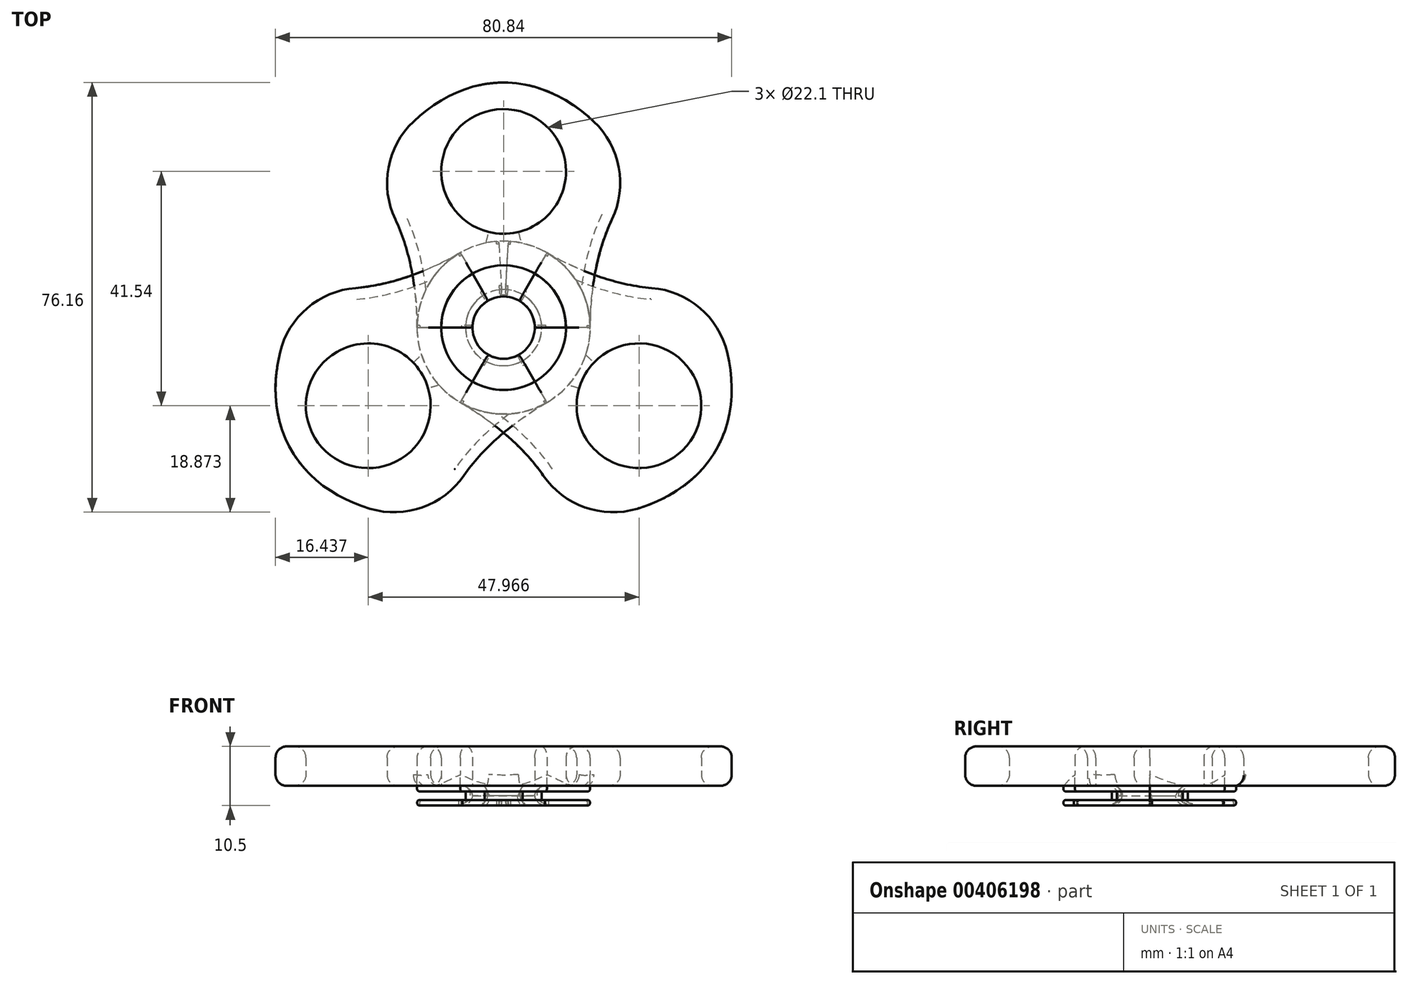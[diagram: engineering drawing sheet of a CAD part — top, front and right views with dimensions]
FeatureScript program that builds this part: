
annotation { "Feature Type Name" : "Feature", "Feature Type Description" : "" }
export const myFeature = defineFeature(function(context is Context, id is Id, definition is map)
    precondition{}
    {
        {
            var Q0;
            Q0=qCreatedBy(makeId("Top.planeOp"),FACE);
            var sketch = newSketch(context, id + "F0", { "sketchPlane" : qUnion([Q0])});
            skCircle(sketch, "E0", {"center": v(0, 0) * mm, "radius": 11.05 * mm});
            skEllipse(sketch, "E1", {"center": v(0, 0) * mm, "majorRadius": 43.44 * mm, "minorRadius": 29.52 * mm, "majorAxis": v(0, 1)});
            skEllipse(sketch, "E2", {"center": v(29.52, 0) * mm, "majorRadius": 28 * mm, "minorRadius": 14.19 * mm, "majorAxis": v(0, -1)});
            skLineSegment(sketch, "E3", {"start": v(0, 58.33) * mm, "end": v(0, -59.11) * mm});
            skEllipse(sketch, "E4", {"center": v(-29.52, 0) * mm, "majorRadius": 27.94 * mm, "minorRadius": 14.94 * mm, "majorAxis": v(0, 1)});
            skCircle(sketch, "E5", {"center": v(0, 27.7) * mm, "radius": 11.05 * mm});
            skLineSegment(sketch, "E6", {"start": v(54.05, 0) * mm, "end": v(-64.12, 0) * mm});
            skCircle(sketch, "E7", {"center": v(0, 0) * mm, "radius": 5.5 * mm});
            skCircle(sketch, "E8", {"center": v(0, 0) * mm, "radius": 15.34 * mm});
            skCircle(sketch, "E9", {"center": v(0, 0) * mm, "radius": 6.75 * mm});
            skSolve(sketch);
        }
        {
            var Q0;
            {var subQ1=sQuery(id+"F0.wireOp",EDGE,"E3");var subQ5=sQuery(id+"F0.wireOp",EDGE,"E0");var subQ6=makeQuery(id+"F0.imprint","INTERSECT",VERTEX,{"disambiguationData":[OD(0.0)],"derivedFrom":[subQ5,subQ1]});Q0=makeQuery(id+"F0.imprint","IMPRINT",FACE,{"disambiguationData":[TD([[makeQuery(id+"F0.imprint","IMPRINT",EDGE,{"disambiguationData":[TD([[subQ6,1.0]])],"derivedFrom":subQ5}),-1.0]])]});}
            var Q1;
            {var subQ1=sQuery(id+"F0.wireOp",EDGE,"E3");var subQ6=sQuery(id+"F0.wireOp",EDGE,"E1");var subQ9=makeQuery(id+"F0.imprint","INTERSECT",VERTEX,{"disambiguationData":[OD(0.0)],"derivedFrom":[subQ6,subQ1]});Q1=makeQuery(id+"F0.imprint","IMPRINT",FACE,{"disambiguationData":[TD([[makeQuery(id+"F0.imprint","IMPRINT",EDGE,{"disambiguationData":[TD([[subQ9,1.0]])],"derivedFrom":subQ6}),1.0]])]});}
            extrude(context, id + "F1", {"entities" : qUnion([Q0, Q1]), "depth" : 7 * mm});
        }
        {
            var Q0;
            {var subQ0=sQuery(id+"F0.wireOp",EDGE,"E3");var subQ1=sQuery(id+"F0.wireOp",EDGE,"E0");var subQ2=makeQuery(id+"F0.imprint","INTERSECT",VERTEX,{"disambiguationData":[OD(0.0)],"derivedFrom":[subQ1,subQ0]});Q0=makeQuery(id+"F0.imprint","IMPRINT",FACE,{"disambiguationData":[TD([[makeQuery(id+"F0.imprint","IMPRINT",EDGE,{"disambiguationData":[TD([[subQ2,1.0]])],"derivedFrom":subQ1}),-1.0]])]});}
            var Q1;
            {var subQ0=sQuery(id+"F0.wireOp",EDGE,"E3");var subQ1=sQuery(id+"F0.wireOp",EDGE,"E0");var subQ2=makeQuery(id+"F0.imprint","INTERSECT",VERTEX,{"disambiguationData":[OD(0.0)],"derivedFrom":[subQ1,subQ0]});Q1=makeQuery(id+"F0.imprint","IMPRINT",FACE,{"disambiguationData":[TD([[makeQuery(id+"F0.imprint","IMPRINT",EDGE,{"disambiguationData":[TD([[subQ2,1.0]])],"derivedFrom":subQ1}),1.0]])]});}
            var Q2;
            {var subQ0=sQuery(id+"F0.wireOp",EDGE,"E9");var subQ1=sQuery(id+"F0.wireOp",EDGE,"E3");var subQ2=makeQuery(id+"F0.imprint","INTERSECT",VERTEX,{"disambiguationData":[OD(0.0)],"derivedFrom":[subQ1,subQ0]});Q2=makeQuery(id+"F0.imprint","IMPRINT",FACE,{"disambiguationData":[TD([[makeQuery(id+"F0.imprint","IMPRINT",EDGE,{"disambiguationData":[TD([[subQ2,-1.0]])],"derivedFrom":subQ1}),1.0]])]});}
            extrude(context, id + "F2", {"entities" : qUnion([Q0, Q1, Q2]), "operationType" : NewBodyOperationType.ADD, "oppositeDirection" : true, "depth" : 1 * mm});
        }
        {
            var Q0;
            {var subQ0=sQuery(id+"F0.wireOp",EDGE,"E9");var subQ1=sQuery(id+"F0.wireOp",EDGE,"E3");var subQ2=makeQuery(id+"F0.imprint","INTERSECT",VERTEX,{"disambiguationData":[OD(0.0)],"derivedFrom":[subQ1,subQ0]});Q0=makeQuery(id+"F0.imprint","IMPRINT",FACE,{"disambiguationData":[TD([[makeQuery(id+"F0.imprint","IMPRINT",EDGE,{"disambiguationData":[TD([[subQ2,-1.0]])],"derivedFrom":subQ1}),1.0]])]});}
            extrude(context, id + "F3", {"entities" : qUnion([Q0]), "operationType" : NewBodyOperationType.ADD, "oppositeDirection" : true, "depth" : 2.5 * mm});
        }
        {
            var Q0;
            {var subQ0=sQuery(id+"F0.wireOp",EDGE,"E9");var subQ1=sQuery(id+"F0.wireOp",EDGE,"E3");var subQ2=makeQuery(id+"F0.imprint","INTERSECT",VERTEX,{"disambiguationData":[OD(0.0)],"derivedFrom":[subQ1,subQ0]});Q0=makeQuery(id+"F0.imprint","IMPRINT",FACE,{"disambiguationData":[TD([[makeQuery(id+"F0.imprint","IMPRINT",EDGE,{"disambiguationData":[TD([[subQ2,-1.0]])],"derivedFrom":subQ1}),1.0]])]});}
            var Q1;
            {var subQ0=sQuery(id+"F0.wireOp",EDGE,"E3");var subQ1=sQuery(id+"F0.wireOp",EDGE,"E0");var subQ2=makeQuery(id+"F0.imprint","INTERSECT",VERTEX,{"disambiguationData":[OD(0.0)],"derivedFrom":[subQ1,subQ0]});Q1=makeQuery(id+"F0.imprint","IMPRINT",FACE,{"disambiguationData":[TD([[makeQuery(id+"F0.imprint","IMPRINT",EDGE,{"disambiguationData":[TD([[subQ2,1.0]])],"derivedFrom":subQ1}),1.0]])]});}
            var Q2;
            {var subQ0=sQuery(id+"F0.wireOp",EDGE,"E3");var subQ1=sQuery(id+"F0.wireOp",EDGE,"E0");var subQ2=makeQuery(id+"F0.imprint","INTERSECT",VERTEX,{"disambiguationData":[OD(0.0)],"derivedFrom":[subQ1,subQ0]});Q2=makeQuery(id+"F0.imprint","IMPRINT",FACE,{"disambiguationData":[TD([[makeQuery(id+"F0.imprint","IMPRINT",EDGE,{"disambiguationData":[TD([[subQ2,1.0]])],"derivedFrom":subQ1}),-1.0]])]});}
            extrude(context, id + "F4", {"entities" : qUnion([Q0, Q1, Q2]), "operationType" : NewBodyOperationType.ADD, "oppositeDirection" : true, "depth" : 3.5 * mm, "hasSecondDirection" : true, "secondDirectionOppositeDirection" : true, "secondDirectionDepth" : 2.5 * mm});
        }
        {
            var Q0;
            Q0=makeQuery(id+"F1.opExtrude","SWEPT_BODY",BODY,{"disambiguationData":[OSD([sQuery(id+"F0.wireOp",EDGE,"E0"),sQuery(id+"F0.wireOp",EDGE,"E1"),sQuery(id+"F0.wireOp",EDGE,"E2"),sQuery(id+"F0.wireOp",EDGE,"E3"),sQuery(id+"F0.wireOp",EDGE,"E5"),sQuery(id+"F0.wireOp",EDGE,"E6")])]});
            var Q1;
            Q1=qCreatedBy(makeId("Right.planeOp"),FACE);
            mirror(context, id + "F5", {"operationType" : NewBodyOperationType.ADD, "entities" : qUnion([Q0]), "mirrorPlane" : qUnion([Q1])});
        }
        {
            var Q0;
            {var subQ0=sQuery(id+"F0.wireOp",EDGE,"E6");var subQ1=sQuery(id+"F0.wireOp",EDGE,"E3");var subQ2=makeQuery(id+"F0.imprint","INTERSECT",VERTEX,{"derivedFrom":[subQ1,subQ0]});Q0=makeQuery(id+"F0.imprint","IMPRINT",FACE,{"disambiguationData":[TD([[makeQuery(id+"F0.imprint","IMPRINT",EDGE,{"disambiguationData":[TD([[subQ2,-1.0]])],"derivedFrom":subQ1}),-1.0]])]});}
            var Q1;
            {var subQ0=sQuery(id+"F0.wireOp",EDGE,"E7");var subQ1=sQuery(id+"F0.wireOp",EDGE,"E3");var subQ2=makeQuery(id+"F0.imprint","INTERSECT",VERTEX,{"disambiguationData":[OD(0.0)],"derivedFrom":[subQ1,subQ0]});Q1=makeQuery(id+"F0.imprint","IMPRINT",FACE,{"disambiguationData":[TD([[makeQuery(id+"F0.imprint","IMPRINT",EDGE,{"disambiguationData":[TD([[subQ2,-1.0]])],"derivedFrom":subQ1}),-1.0]])]});}
            var Q2;
            {var subQ0=sQuery(id+"F0.wireOp",EDGE,"E7");var subQ1=sQuery(id+"F0.wireOp",EDGE,"E3");var subQ2=makeQuery(id+"F0.imprint","INTERSECT",VERTEX,{"disambiguationData":[OD(0.0)],"derivedFrom":[subQ1,subQ0]});Q2=makeQuery(id+"F0.imprint","IMPRINT",FACE,{"disambiguationData":[TD([[makeQuery(id+"F0.imprint","IMPRINT",EDGE,{"disambiguationData":[TD([[subQ2,-1.0]])],"derivedFrom":subQ1}),1.0]])]});}
            var Q3;
            {var subQ0=sQuery(id+"F0.wireOp",EDGE,"E6");var subQ1=sQuery(id+"F0.wireOp",EDGE,"E3");var subQ2=makeQuery(id+"F0.imprint","INTERSECT",VERTEX,{"derivedFrom":[subQ1,subQ0]});Q3=makeQuery(id+"F0.imprint","IMPRINT",FACE,{"disambiguationData":[TD([[makeQuery(id+"F0.imprint","IMPRINT",EDGE,{"disambiguationData":[TD([[subQ2,-1.0]])],"derivedFrom":subQ1}),1.0]])]});}
            extrude(context, id + "F6", {"entities" : qUnion([Q0, Q1, Q2, Q3]), "depth" : 22.66 * mm, "hasSecondDirection" : true, "secondDirectionOppositeDirection" : false, "secondDirectionDepth" : 15.2 * mm});
        }
        {
            var Q0;
            {var subQ0=makeQuery(id+"F4.opExtrude","CAP_FACE",FACE,{"disambiguationData":[OSD([sQuery(id+"F0.wireOp",EDGE,"E3"),sQuery(id+"F0.wireOp",EDGE,"E6"),sQuery(id+"F0.wireOp",EDGE,"E7"),sQuery(id+"F0.wireOp",EDGE,"E8")])],"isStart":false});Q0=makeQuery(id+"F5.boolean.opBoolean","MERGE",FACE,{"derivedFrom":[subQ0,makeQuery(id+"F5.opPattern","COPY",FACE,{"derivedFrom":subQ0,"instanceName":"1"})]});}
            var sketch = newSketch(context, id + "F7", { "sketchPlane" : qUnion([Q0])});
            skLineSegment(sketch, "E10", {"start": v(0, -18) * mm, "end": v(-1, -18) * mm});
            skLineSegment(sketch, "E11", {"start": v(-1, -18) * mm, "end": v(0, 0) * mm});
            skLineSegment(sketch, "E12", {"start": v(0, 0) * mm, "end": v(1, -18) * mm});
            skLineSegment(sketch, "E13", {"start": v(1, -18) * mm, "end": v(0, -18) * mm});
            skSolve(sketch);
        }
        {
            var Q0;
            {var subQ0=makeQuery(id+"F1.opExtrude","CAP_EDGE",EDGE,{"disambiguationData":[OSD([sQuery(id+"F0.wireOp",EDGE,"E5")])],"isStart":true});Q0=makeQuery(id+"F5.boolean.opBoolean","MERGE",EDGE,{"derivedFrom":[subQ0,makeQuery(id+"F5.opPattern","COPY",EDGE,{"derivedFrom":subQ0,"instanceName":"1"})]});}
            var Q1;
            Q1=makeQuery(id+"F1.opExtrude","CAP_EDGE",EDGE,{"disambiguationData":[OSD([sQuery(id+"F0.wireOp",EDGE,"E2")])],"isStart":true});
            var Q2;
            Q2=makeQuery(id+"F1.opExtrude","CAP_EDGE",EDGE,{"disambiguationData":[OSD([sQuery(id+"F0.wireOp",EDGE,"E2")])],"isStart":false});
            var Q3;
            Q3=makeQuery(id+"F5.opPattern","COPY",EDGE,{"derivedFrom":makeQuery(id+"F1.opExtrude","CAP_EDGE",EDGE,{"disambiguationData":[OSD([sQuery(id+"F0.wireOp",EDGE,"E2")])],"isStart":true}),"instanceName":"1"});
            var Q4;
            {var subQ0=makeQuery(id+"F1.opExtrude","CAP_EDGE",EDGE,{"disambiguationData":[OSD([sQuery(id+"F0.wireOp",EDGE,"E1")])],"isStart":true});Q4=makeQuery(id+"F5.boolean.opBoolean","MERGE",EDGE,{"derivedFrom":[subQ0,makeQuery(id+"F5.opPattern","COPY",EDGE,{"derivedFrom":subQ0,"instanceName":"1"})]});}
            var Q5;
            {var subQ0=makeQuery(id+"F4.opExtrude","CAP_EDGE",EDGE,{"disambiguationData":[OSD([sQuery(id+"F0.wireOp",EDGE,"E7")])],"isStart":false});Q5=makeQuery(id+"F5.boolean.opBoolean","MERGE",EDGE,{"derivedFrom":[subQ0,makeQuery(id+"F5.opPattern","COPY",EDGE,{"derivedFrom":subQ0,"instanceName":"1"})]});}
            var Q6;
            {var subQ0=makeQuery(id+"F2.opExtrude","CAP_EDGE",EDGE,{"disambiguationData":[OSD([sQuery(id+"F0.wireOp",EDGE,"E7")])],"isStart":true});Q6=makeQuery(id+"F5.boolean.opBoolean","MERGE",EDGE,{"derivedFrom":[subQ0,makeQuery(id+"F5.opPattern","COPY",EDGE,{"derivedFrom":subQ0,"instanceName":"1"})]});}
            var Q7;
            {var subQ0=makeQuery(id+"F1.opExtrude","CAP_EDGE",EDGE,{"disambiguationData":[OSD([sQuery(id+"F0.wireOp",EDGE,"E1")])],"isStart":false});Q7=makeQuery(id+"F5.boolean.opBoolean","MERGE",EDGE,{"derivedFrom":[subQ0,makeQuery(id+"F5.opPattern","COPY",EDGE,{"derivedFrom":subQ0,"instanceName":"1"})]});}
            var Q8;
            {var subQ0=makeQuery(id+"F1.opExtrude","CAP_EDGE",EDGE,{"disambiguationData":[OSD([sQuery(id+"F0.wireOp",EDGE,"E5")])],"isStart":false});Q8=makeQuery(id+"F5.boolean.opBoolean","MERGE",EDGE,{"derivedFrom":[subQ0,makeQuery(id+"F5.opPattern","COPY",EDGE,{"derivedFrom":subQ0,"instanceName":"1"})]});}
            var Q9;
            {var subQ0=makeQuery(id+"F1.opExtrude","CAP_EDGE",EDGE,{"disambiguationData":[OSD([sQuery(id+"F0.wireOp",EDGE,"E0")])],"isStart":false});Q9=makeQuery(id+"F5.boolean.opBoolean","MERGE",EDGE,{"derivedFrom":[subQ0,makeQuery(id+"F5.opPattern","COPY",EDGE,{"derivedFrom":subQ0,"instanceName":"1"})]});}
            var Q10;
            Q10=makeQuery(id+"F5.opPattern","COPY",EDGE,{"derivedFrom":makeQuery(id+"F1.opExtrude","CAP_EDGE",EDGE,{"disambiguationData":[OSD([sQuery(id+"F0.wireOp",EDGE,"E2")])],"isStart":false}),"instanceName":"1"});
            fillet(context, id + "F8", {"entities" : qUnion([Q0, Q1, Q2, Q3, Q4, Q5, Q6, Q7, Q8, Q9, Q10]), "radius" : 2 * mm, "tangentPropagation" : true, "allowEdgeOverflow" : false});
        }
        {
            var Q0;
            Q0=makeQuery(id+"F5.opPattern","COPY",EDGE,{"derivedFrom":makeQuery(id+"F1.opExtrude","SWEPT_EDGE",EDGE,{"disambiguationData":[OSD([sQuery(id+"F0.wireOp",EDGE,"E1"),sQuery(id+"F0.wireOp",EDGE,"E2")])]}),"instanceName":"1"});
            var Q1;
            Q1=makeQuery(id+"F1.opExtrude","SWEPT_EDGE",EDGE,{"disambiguationData":[OSD([sQuery(id+"F0.wireOp",EDGE,"E1"),sQuery(id+"F0.wireOp",EDGE,"E2")])]});
            fillet(context, id + "F9", {"entities" : qUnion([Q0, Q1]), "radius" : 15 * mm, "tangentPropagation" : true, "allowEdgeOverflow" : false});
        }
        {
            var Q0;
            {var subQ0=makeQuery(id+"F4.opExtrude","CAP_EDGE",EDGE,{"disambiguationData":[OSD([sQuery(id+"F0.wireOp",EDGE,"E8")])],"isStart":false});Q0=makeQuery(id+"F5.boolean.opBoolean","MERGE",EDGE,{"derivedFrom":[subQ0,makeQuery(id+"F5.opPattern","COPY",EDGE,{"derivedFrom":subQ0,"instanceName":"1"})]});}
            var Q1;
            {var subQ0=makeQuery(id+"F2.opExtrude","CAP_EDGE",EDGE,{"disambiguationData":[OSD([sQuery(id+"F0.wireOp",EDGE,"E8")])],"isStart":false});Q1=makeQuery(id+"F5.boolean.opBoolean","MERGE",EDGE,{"derivedFrom":[subQ0,makeQuery(id+"F5.opPattern","COPY",EDGE,{"derivedFrom":subQ0,"instanceName":"1"})]});}
            var Q2;
            {var subQ0=makeQuery(id+"F4.opExtrude","CAP_EDGE",EDGE,{"disambiguationData":[OSD([sQuery(id+"F0.wireOp",EDGE,"E8")])],"isStart":true});Q2=makeQuery(id+"F5.boolean.opBoolean","MERGE",EDGE,{"derivedFrom":[subQ0,makeQuery(id+"F5.opPattern","COPY",EDGE,{"derivedFrom":subQ0,"instanceName":"1"})]});}
            var Q3;
            {var subQ0=makeQuery(id+"F2.opExtrude","CAP_EDGE",EDGE,{"disambiguationData":[OSD([sQuery(id+"F0.wireOp",EDGE,"E8")])],"isStart":true});Q3=makeQuery(id+"F5.boolean.opBoolean","MERGE",EDGE,{"derivedFrom":[subQ0,makeQuery(id+"F5.opPattern","COPY",EDGE,{"derivedFrom":subQ0,"instanceName":"1"})]});}
            var Q4;
            {var subQ0=makeQuery(id+"F2.opExtrude","CAP_EDGE",EDGE,{"disambiguationData":[OSD([sQuery(id+"F0.wireOp",EDGE,"E8")])],"isStart":true});Q4=makeQuery(id+"F5.boolean.opBoolean","MERGE",EDGE,{"derivedFrom":[subQ0,makeQuery(id+"F5.opPattern","COPY",EDGE,{"derivedFrom":subQ0,"instanceName":"1"})]});}
            fillet(context, id + "F10", {"entities" : qUnion([Q0, Q1, Q2, Q3, Q4]), "radius" : 0.5 * mm, "tangentPropagation" : true, "allowEdgeOverflow" : false});
        }
        {
            var Q0;
            Q0=makeQuery(id+"F1.opExtrude","SWEPT_BODY",BODY,{"disambiguationData":[OSD([sQuery(id+"F0.wireOp",EDGE,"E0"),sQuery(id+"F0.wireOp",EDGE,"E1"),sQuery(id+"F0.wireOp",EDGE,"E2"),sQuery(id+"F0.wireOp",EDGE,"E3"),sQuery(id+"F0.wireOp",EDGE,"E5"),sQuery(id+"F0.wireOp",EDGE,"E6")])]});
            var Q1;
            Q1=makeQuery(id+"F6.opExtrude","CAP_EDGE",EDGE,{"disambiguationData":[OSD([sQuery(id+"F0.wireOp",EDGE,"E7")])],"isStart":true});
            circularPattern(context, id + "F11", {"operationType" : NewBodyOperationType.ADD, "entities" : qUnion([Q0]), "axis" : qUnion([Q1]), "angle" : 360 * degree, "instanceCount" : 3, "equalSpace" : true});
        }
        {
            var Q0;
            {var subQ0=sQuery(id+"F7.wireOp",EDGE,"E11");var subQ1=makeQuery(id+"F4.opExtrude","CAP_EDGE",EDGE,{"disambiguationData":[OSD([sQuery(id+"F0.wireOp",EDGE,"E8")])],"isStart":false});var subQ2=makeQuery(id+"F5.boolean.opBoolean","MERGE",EDGE,{"derivedFrom":[subQ1,makeQuery(id+"F5.opPattern","COPY",EDGE,{"derivedFrom":subQ1,"instanceName":"1"})]});var subQ3=makeQuery(id+"F7.imprint","INTERSECT",VERTEX,{"derivedFrom":[subQ2,subQ0]});Q0=makeQuery(id+"F7.imprint","IMPRINT",FACE,{"disambiguationData":[TD([[makeQuery(id+"F7.imprint","IMPRINT",EDGE,{"disambiguationData":[TD([[subQ3,-1.0]])],"derivedFrom":subQ0}),-1.0]])]});}
            extrude(context, id + "F12", {"entities" : qUnion([Q0]), "operationType" : NewBodyOperationType.REMOVE, "oppositeDirection" : true, "depth" : 1 * mm});
        }
        {
            var Q0;
            {var subQ0=sQuery(id+"F0.wireOp",EDGE,"E8");var subQ3=sQuery(id+"F0.wireOp",EDGE,"E7");var subQ6=makeQuery(id+"F4.opExtrude","CAP_FACE",FACE,{"disambiguationData":[OSD([sQuery(id+"F0.wireOp",EDGE,"E3"),sQuery(id+"F0.wireOp",EDGE,"E6"),subQ3,subQ0])],"isStart":false});var subQ7=makeQuery(id+"F5.boolean.opBoolean","MERGE",FACE,{"derivedFrom":[subQ6,makeQuery(id+"F5.opPattern","COPY",FACE,{"derivedFrom":subQ6,"instanceName":"1"})]});Q0=makeQuery(id+"FEYc9VW4fI0q4IH_2.1.F12.boolean.opBoolean","SPLIT",FACE,{"disambiguationData":[TD([makeQuery(id+"F12.boolean.opBoolean","COPY",FACE,{"derivedFrom":makeQuery(id+"F12.opExtrude","SWEPT_FACE",FACE,{"disambiguationData":[OSD([sQuery(id+"F7.wireOp",EDGE,"E12")])]})})])],"derivedFrom":makeQuery(id+"F11.boolean.opBoolean","MERGE",FACE,{"derivedFrom":[subQ7,makeQuery(id+"F11.opPattern","COPY",FACE,{"derivedFrom":subQ7,"instanceName":"1"}),makeQuery(id+"F11.opPattern","COPY",FACE,{"derivedFrom":subQ7,"instanceName":"2"}),makeQuery(id+"F11.opPattern","COPY",FACE,{"derivedFrom":subQ7,"instanceName":"3"})]})});}
            var Q1;
            {var subQ0=sQuery(id+"F0.wireOp",EDGE,"E8");var subQ6=sQuery(id+"F0.wireOp",EDGE,"E7");var subQ12=makeQuery(id+"FEYc9VW4fI0q4IH_2.1.F12.opExtrude","SWEPT_FACE",FACE,{"disambiguationData":[OSD([sQuery(id+"F7.wireOp",EDGE,"E12")])]});var subQ13=sQuery(id+"F7.wireOp",EDGE,"E11");var subQ14=makeQuery(id+"F4.opExtrude","CAP_FACE",FACE,{"disambiguationData":[OSD([sQuery(id+"F0.wireOp",EDGE,"E3"),sQuery(id+"F0.wireOp",EDGE,"E6"),subQ6,subQ0])],"isStart":false});var subQ15=makeQuery(id+"F5.boolean.opBoolean","MERGE",FACE,{"derivedFrom":[subQ14,makeQuery(id+"F5.opPattern","COPY",FACE,{"derivedFrom":subQ14,"instanceName":"1"})]});Q1=makeQuery(id+"FEYc9VW4fI0q4IH_2.2.F12.boolean.opBoolean","SPLIT",FACE,{"disambiguationData":[TD([makeQuery(id+"FEYc9VW4fI0q4IH_2.1.F12.boolean.opBoolean","COPY",FACE,{"derivedFrom":subQ12})])],"derivedFrom":makeQuery(id+"FEYc9VW4fI0q4IH_2.1.F12.boolean.opBoolean","SPLIT",FACE,{"disambiguationData":[TD([makeQuery(id+"F12.boolean.opBoolean","COPY",FACE,{"derivedFrom":makeQuery(id+"F12.opExtrude","SWEPT_FACE",FACE,{"disambiguationData":[OSD([subQ13])]})})])],"derivedFrom":makeQuery(id+"F11.boolean.opBoolean","MERGE",FACE,{"derivedFrom":[subQ15,makeQuery(id+"F11.opPattern","COPY",FACE,{"derivedFrom":subQ15,"instanceName":"1"}),makeQuery(id+"F11.opPattern","COPY",FACE,{"derivedFrom":subQ15,"instanceName":"2"}),makeQuery(id+"F11.opPattern","COPY",FACE,{"derivedFrom":subQ15,"instanceName":"3"})]})})});}
            var Q2;
            {var subQ0=sQuery(id+"F0.wireOp",EDGE,"E8");var subQ6=sQuery(id+"F7.wireOp",EDGE,"E12");var subQ7=makeQuery(id+"FEYc9VW4fI0q4IH_2.2.F12.opExtrude","SWEPT_FACE",FACE,{"disambiguationData":[OSD([subQ6])]});var subQ8=sQuery(id+"F0.wireOp",EDGE,"E7");var subQ14=sQuery(id+"F7.wireOp",EDGE,"E11");var subQ15=makeQuery(id+"F12.boolean.opBoolean","COPY",FACE,{"derivedFrom":makeQuery(id+"F12.opExtrude","SWEPT_FACE",FACE,{"disambiguationData":[OSD([subQ14])]})});var subQ16=makeQuery(id+"F4.opExtrude","CAP_FACE",FACE,{"disambiguationData":[OSD([sQuery(id+"F0.wireOp",EDGE,"E3"),sQuery(id+"F0.wireOp",EDGE,"E6"),subQ8,subQ0])],"isStart":false});var subQ17=makeQuery(id+"F5.boolean.opBoolean","MERGE",FACE,{"derivedFrom":[subQ16,makeQuery(id+"F5.opPattern","COPY",FACE,{"derivedFrom":subQ16,"instanceName":"1"})]});Q2=makeQuery(id+"FEYc9VW4fI0q4IH_2.3.F12.boolean.opBoolean","SPLIT",FACE,{"disambiguationData":[TD([makeQuery(id+"FEYc9VW4fI0q4IH_2.2.F12.boolean.opBoolean","COPY",FACE,{"derivedFrom":subQ7})])],"derivedFrom":makeQuery(id+"FEYc9VW4fI0q4IH_2.2.F12.boolean.opBoolean","SPLIT",FACE,{"disambiguationData":[TD([subQ15])],"derivedFrom":makeQuery(id+"FEYc9VW4fI0q4IH_2.1.F12.boolean.opBoolean","SPLIT",FACE,{"disambiguationData":[TD([subQ15])],"derivedFrom":makeQuery(id+"F11.boolean.opBoolean","MERGE",FACE,{"derivedFrom":[subQ17,makeQuery(id+"F11.opPattern","COPY",FACE,{"derivedFrom":subQ17,"instanceName":"1"}),makeQuery(id+"F11.opPattern","COPY",FACE,{"derivedFrom":subQ17,"instanceName":"2"}),makeQuery(id+"F11.opPattern","COPY",FACE,{"derivedFrom":subQ17,"instanceName":"3"})]})})})});}
            var Q3;
            {var subQ0=sQuery(id+"F0.wireOp",EDGE,"E8");var subQ6=makeQuery(id+"F12.boolean.opBoolean","COPY",FACE,{"derivedFrom":makeQuery(id+"F12.opExtrude","SWEPT_FACE",FACE,{"disambiguationData":[OSD([sQuery(id+"F7.wireOp",EDGE,"E11")])]})});var subQ7=sQuery(id+"F0.wireOp",EDGE,"E7");var subQ14=makeQuery(id+"F4.opExtrude","CAP_FACE",FACE,{"disambiguationData":[OSD([sQuery(id+"F0.wireOp",EDGE,"E3"),sQuery(id+"F0.wireOp",EDGE,"E6"),subQ7,subQ0])],"isStart":false});var subQ15=makeQuery(id+"F5.boolean.opBoolean","MERGE",FACE,{"derivedFrom":[subQ14,makeQuery(id+"F5.opPattern","COPY",FACE,{"derivedFrom":subQ14,"instanceName":"1"})]});Q3=makeQuery(id+"FEYc9VW4fI0q4IH_2.3.F12.boolean.opBoolean","SPLIT",FACE,{"disambiguationData":[TD([subQ6])],"derivedFrom":makeQuery(id+"FEYc9VW4fI0q4IH_2.2.F12.boolean.opBoolean","SPLIT",FACE,{"disambiguationData":[TD([subQ6])],"derivedFrom":makeQuery(id+"FEYc9VW4fI0q4IH_2.1.F12.boolean.opBoolean","SPLIT",FACE,{"disambiguationData":[TD([subQ6])],"derivedFrom":makeQuery(id+"F11.boolean.opBoolean","MERGE",FACE,{"derivedFrom":[subQ15,makeQuery(id+"F11.opPattern","COPY",FACE,{"derivedFrom":subQ15,"instanceName":"1"}),makeQuery(id+"F11.opPattern","COPY",FACE,{"derivedFrom":subQ15,"instanceName":"2"}),makeQuery(id+"F11.opPattern","COPY",FACE,{"derivedFrom":subQ15,"instanceName":"3"})]})})})});}
            fillet(context, id + "F13", {"entities" : qUnion([Q0, Q1, Q2, Q3]), "radius" : 0.4 * mm, "tangentPropagation" : true, "allowEdgeOverflow" : false});
        }
        {
            var Q0;
            Q0=makeQuery(id+"F6.opExtrude","SWEPT_BODY",BODY,{"disambiguationData":[OSD([sQuery(id+"F0.wireOp",EDGE,"E7")])]});
            deleteBodies(context, id + "F14", {"entities" : qUnion([Q0])});
        }
    });
